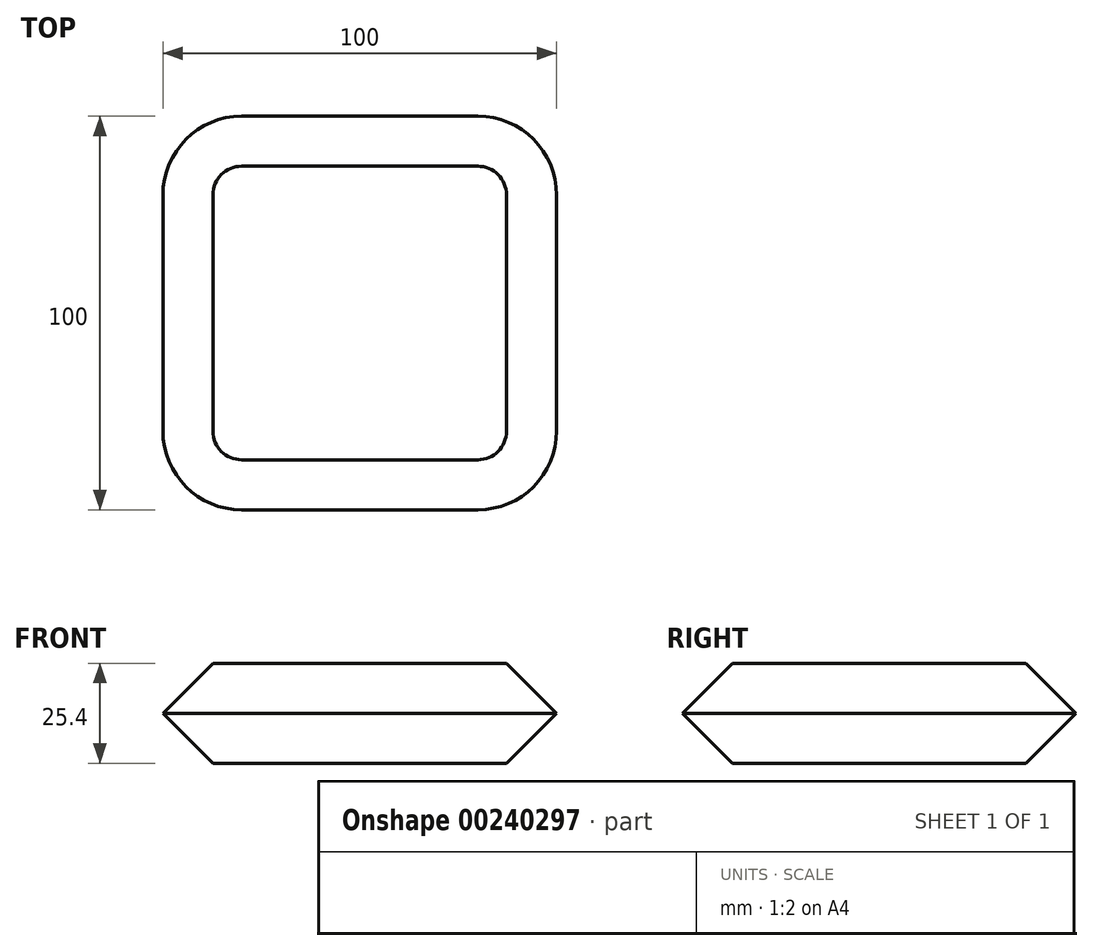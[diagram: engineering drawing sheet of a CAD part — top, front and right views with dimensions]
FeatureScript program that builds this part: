
annotation { "Feature Type Name" : "Feature", "Feature Type Description" : "" }
export const myFeature = defineFeature(function(context is Context, id is Id, definition is map)
    precondition{}
    {
        {
            var Q0;
            Q0=qCreatedBy(makeId("Top.planeOp"),FACE);
            var sketch = newSketch(context, id + "F0", { "sketchPlane" : qUnion([Q0])});
            skLineSegment(sketch, "E0.bottom", {"start": v(30, -50) * mm, "end": v(-30, -50) * mm});
            skLineSegment(sketch, "E0.top", {"start": v(30, 50) * mm, "end": v(-30, 50) * mm});
            skLineSegment(sketch, "E0.left", {"start": v(50, -30) * mm, "end": v(50, 30) * mm});
            skLineSegment(sketch, "E0.right", {"start": v(-50, -30) * mm, "end": v(-50, 30) * mm});
            skPoint(sketch, "E0.middle", {"position": v(0, 0) * mm});
            skPoint(sketch, "E1.visualSharp", {"position": v(-50, 50) * mm});
            skArc(sketch, "E1.filletArc", {"start": v(-30, 50) * mm, "mid": v(-44.14, 44.14) * mm, "end": v(-50, 30) * mm});
            skPoint(sketch, "E2.visualSharp", {"position": v(50, 50) * mm});
            skArc(sketch, "E2.filletArc", {"start": v(50, 30) * mm, "mid": v(44.14, 44.14) * mm, "end": v(30, 50) * mm});
            skPoint(sketch, "E3.visualSharp", {"position": v(50, -50) * mm});
            skArc(sketch, "E3.filletArc", {"start": v(30, -50) * mm, "mid": v(44.14, -44.14) * mm, "end": v(50, -30) * mm});
            skPoint(sketch, "E4.visualSharp", {"position": v(-50, -50) * mm});
            skArc(sketch, "E4.filletArc", {"start": v(-50, -30) * mm, "mid": v(-44.14, -44.14) * mm, "end": v(-30, -50) * mm});
            skSolve(sketch);
        }
        {
            var Q0;
            Q0=makeQuery(id+"F0.imprint","IMPRINT",FACE,{"disambiguationData":[TD([[makeQuery(id+"F0.imprint","IMPRINT",EDGE,{"derivedFrom":sQuery(id+"F0.wireOp",EDGE,"E0.bottom")}),-1.0]])]});
            extrude(context, id + "F1", {"entities" : qUnion([Q0]), "depth" : 25.4 * mm});
        }
        {
            var Q0;
            Q0=makeQuery(id+"F1.opExtrude","CAP_FACE",FACE,{"disambiguationData":[OSD([sQuery(id+"F0.wireOp",EDGE,"E0.bottom"),sQuery(id+"F0.wireOp",EDGE,"E0.top"),sQuery(id+"F0.wireOp",EDGE,"E0.left"),sQuery(id+"F0.wireOp",EDGE,"E0.right"),sQuery(id+"F0.wireOp",EDGE,"E1.filletArc"),sQuery(id+"F0.wireOp",EDGE,"E2.filletArc"),sQuery(id+"F0.wireOp",EDGE,"E3.filletArc"),sQuery(id+"F0.wireOp",EDGE,"E4.filletArc")])],"isStart":false});
            chamfer(context, id + "F2", {"entities" : qUnion([Q0]), "width" : 12.7 * mm, "tangentPropagation" : true});
        }
        {
            var Q0;
            Q0=makeQuery(id+"F1.opExtrude","CAP_FACE",FACE,{"disambiguationData":[OSD([sQuery(id+"F0.wireOp",EDGE,"E0.bottom"),sQuery(id+"F0.wireOp",EDGE,"E0.top"),sQuery(id+"F0.wireOp",EDGE,"E0.left"),sQuery(id+"F0.wireOp",EDGE,"E0.right"),sQuery(id+"F0.wireOp",EDGE,"E1.filletArc"),sQuery(id+"F0.wireOp",EDGE,"E2.filletArc"),sQuery(id+"F0.wireOp",EDGE,"E3.filletArc"),sQuery(id+"F0.wireOp",EDGE,"E4.filletArc")])],"isStart":true});
            chamfer(context, id + "F3", {"entities" : qUnion([Q0]), "width" : 12.7 * mm, "tangentPropagation" : true});
        }
    });
